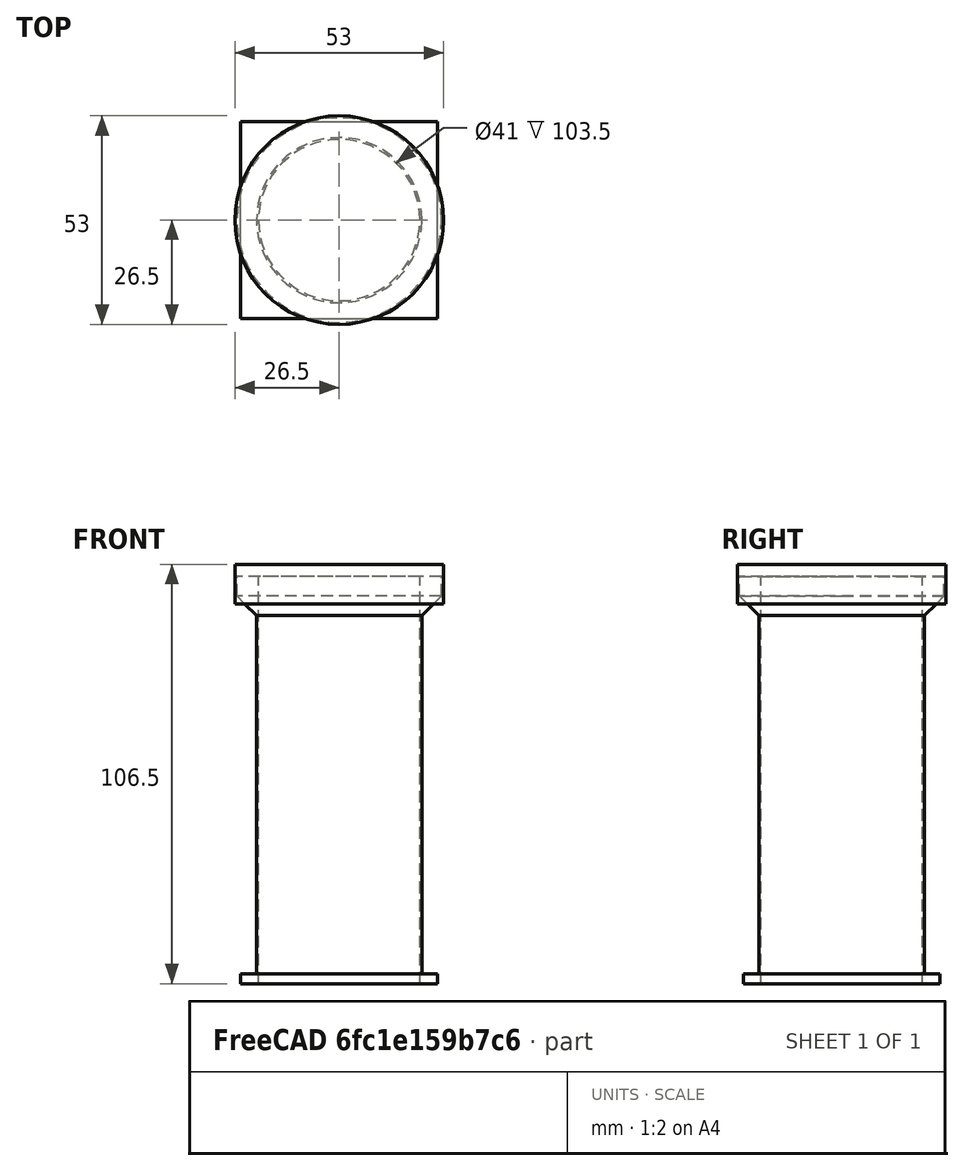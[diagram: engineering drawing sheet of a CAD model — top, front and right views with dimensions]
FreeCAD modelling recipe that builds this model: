
FCSTD DOCUMENT  (FreeCAD 0.19R24366 (Git))
Label: transfer_tunnel
License: All rights reserved
LicenseURL: http://en.wikipedia.org/wiki/All_rights_reserved
objects: Part::Cylinder×4, Part::MultiFuse×2, Mesh::Feature×1, Part::Feature×1, Part::Box×1, Part::Chamfer×1, Part::Cut×1
note: 10 computed .brp shape members not serialized (recipe doc carries the construction recipe); baked Part::Feature solids carry a one-line shape summary decoded from their .brp

FEATURE [Mesh::Feature] transfer_tunnel
FEATURE [Part::Feature] transfer_tunnel001
  Placement = pos=(-13,77,-17) rot=(0,0,1;0rad)
  shape: bbox 51.8 x 51.78 x 103.7 mm, 4306 faces, 0 solids (baked)
FEATURE [Part::Box] Box  label="Cube"
  AttacherType = Attacher::AttachEngine3D
  Height = 2.5
  Length = 50
  Width = 50
FEATURE [Part::Cylinder] Cylinder
  Angle = 360
  AttacherType = Attacher::AttachEngine3D
  Height = 120
  Placement = pos=(25,25,0) rot=(0,0,1;0rad)
  Radius = 20.5
FEATURE [Part::Cylinder] Cylinder001
  Angle = 360
  AttacherType = Attacher::AttachEngine3D
  Height = 100
  Placement = pos=(25,25,0) rot=(0,0,1;0rad)
  Radius = 21
FEATURE [Part::Cylinder] Cylinder002
  Angle = 360
  AttacherType = Attacher::AttachEngine3D
  Height = 10
  Placement = pos=(25,25,93.5) rot=(0,0,1;0rad)
  Radius = 26
FEATURE [Part::Cylinder] Cylinder003
  Angle = 360
  AttacherType = Attacher::AttachEngine3D
  Height = 10
  Placement = pos=(25,25,96.5) rot=(0,0,1;0rad)
  Radius = 26.5
FEATURE [Part::Chamfer] Chamfer
  Base = -> Cylinder002
  Edges = 1 edges r=5: [Edge3]
FEATURE [Part::MultiFuse] Fusion
  Shapes = -> [Cylinder001,Chamfer]
FEATURE [Part::MultiFuse] Fusion001
  Shapes = -> [Box,Fusion]
FEATURE [Part::Cut] Cut
  Base = -> Fusion001
  Tool = -> Cylinder
